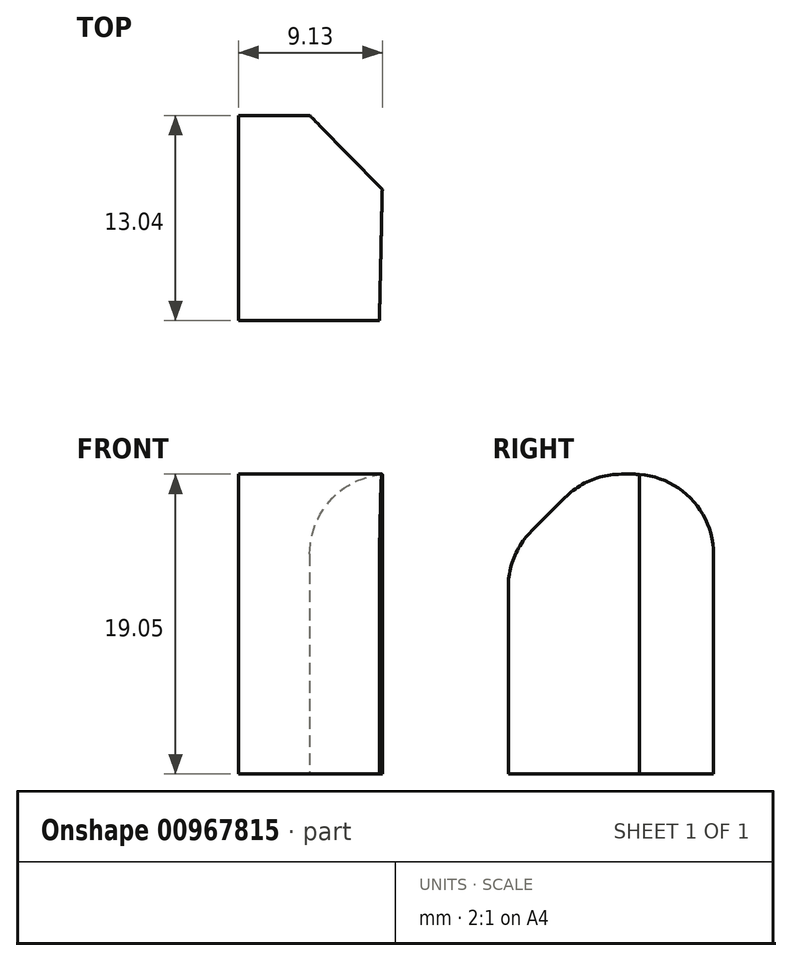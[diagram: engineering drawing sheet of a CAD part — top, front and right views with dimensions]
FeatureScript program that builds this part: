
annotation { "Feature Type Name" : "Feature", "Feature Type Description" : "" }
export const myFeature = defineFeature(function(context is Context, id is Id, definition is map)
    precondition{}
    {
        {
            var Q0;
            Q0=qCreatedBy(makeId("Top.planeOp"),FACE);
            var sketch = newSketch(context, id + "F0", { "sketchPlane" : qUnion([Q0])});
            skLineSegment(sketch, "E0", {"start": v(0, -3.64) * mm, "end": v(0, -16.68) * mm});
            skLineSegment(sketch, "E1", {"start": v(0, -16.68) * mm, "end": v(8.94, -16.68) * mm});
            skLineSegment(sketch, "E2", {"start": v(1.95, -3.64) * mm, "end": v(4.52, -3.64) * mm});
            skLineSegment(sketch, "E3", {"start": v(4.52, -3.64) * mm, "end": v(9.13, -8.34) * mm});
            skPoint(sketch, "E3.endSnap0", {"position": v(4.47, -8.34) * mm});
            skLineSegment(sketch, "E4", {"start": v(9.13, -8.34) * mm, "end": v(8.94, -16.68) * mm});
            skLineSegment(sketch, "E5", {"start": v(1.95, -3.64) * mm, "end": v(0, -3.64) * mm});
            skPoint(sketch, "E6.end.orphan", {"position": v(0, 0) * mm});
            skSolve(sketch);
        }
        {
            var Q0;
            Q0 = qSketchRegion(id + "F0", true);
            extrude(context, id + "F1", {"entities" : qUnion([Q0]), "depth" : 19.05 * mm, "offsetDistance" : 25.4 * mm});
        }
        {
            var Q0;
            Q0 = qSketchRegion(id + "F0", true);
            extrude(context, id + "F2", {"entities" : qUnion([Q0]), "operationType" : NewBodyOperationType.ADD, "depth" : 12.7 * mm, "offsetDistance" : 25.4 * mm});
        }
        {
            var Q0;
            Q0=makeQuery(id+"F1.opExtrude","CAP_EDGE",EDGE,{"disambiguationData":[OSD([sQuery(id+"F0.wireOp",EDGE,"E1")])],"isStart":false});
            chamfer(context, id + "F3", {"entities" : qUnion([Q0]), "width" : 5.08 * mm, "tangentPropagation" : true});
        }
        {
            var Q0;
            {var subQ0=sQuery(id+"F0.wireOp",EDGE,"E1");Q0=makeQuery(id+"F3.opChamfer","BLEND_EDGE",EDGE,{"blendedFrom":[makeQuery(id+"F1.opExtrude","CAP_EDGE",EDGE,{"disambiguationData":[OSD([subQ0])],"isStart":false}),makeQuery(id+"F1.opExtrude","CAP_FACE",FACE,{"disambiguationData":[OSD([sQuery(id+"F0.wireOp",EDGE,"E0"),subQ0,sQuery(id+"F0.wireOp",EDGE,"E2"),sQuery(id+"F0.wireOp",EDGE,"E3"),sQuery(id+"F0.wireOp",EDGE,"E4"),sQuery(id+"F0.wireOp",EDGE,"E5")])],"isStart":false})],"blendedInto":[makeQuery(id+"F1.opExtrude","CAP_FACE",FACE,{"disambiguationData":[OSD([sQuery(id+"F0.wireOp",EDGE,"E0"),subQ0,sQuery(id+"F0.wireOp",EDGE,"E2"),sQuery(id+"F0.wireOp",EDGE,"E3"),sQuery(id+"F0.wireOp",EDGE,"E4"),sQuery(id+"F0.wireOp",EDGE,"E5")])],"isStart":false})]});}
            var Q1;
            {var subQ0=sQuery(id+"F0.wireOp",EDGE,"E1");Q1=makeQuery(id+"F3.opChamfer","BLEND_EDGE",EDGE,{"blendedFrom":[makeQuery(id+"F1.opExtrude","CAP_EDGE",EDGE,{"disambiguationData":[OSD([subQ0])],"isStart":false}),makeQuery(id+"F1.opExtrude","SWEPT_FACE",FACE,{"disambiguationData":[OSD([subQ0])]})],"blendedInto":[makeQuery(id+"F1.opExtrude","SWEPT_FACE",FACE,{"disambiguationData":[OSD([subQ0])]})]});}
            var Q2;
            Q2=makeQuery(id+"F1.opExtrude","CAP_EDGE",EDGE,{"disambiguationData":[OSD([sQuery(id+"F0.wireOp",EDGE,"E2"),sQuery(id+"F0.wireOp",EDGE,"E5")])],"isStart":false});
            fillet(context, id + "F4", {"entities" : qUnion([Q0, Q1, Q2]), "radius" : 5.08 * mm, "tangentPropagation" : true, "allowEdgeOverflow" : false});
        }
    });
